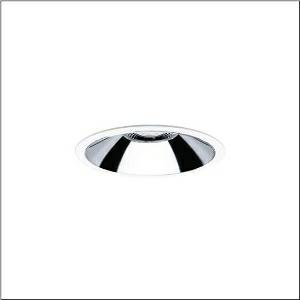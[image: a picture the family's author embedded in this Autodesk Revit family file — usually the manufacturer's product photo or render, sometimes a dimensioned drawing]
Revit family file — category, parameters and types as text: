
# Revit family: lunis_21_xl_51db15df42
name_source: partatom
category: Lighting Fixtures
units: mm (PartAtom-declared; Revit-internal decimal feet)

## family parameters
Cut with Voids When Loaded = No
Host = Face
Light Source = No
Part Type = Normal
Room Calculation Point = No
Round Connector Dimension = Use Diameter
Shared = No

## types (1)
- Lunis 21 XL (1 x LED, 2280 lm, 17.7 W, 4000K)
    Apparent Load = 18 VA
    CIE Flux Codes = 89 99 100 100 100
    Color Rendering = 80
    Color Temperature = 4000K
    Default Elevation = 1800 mm
    Description = Lunis 21,  XL, downlight, of PC, light emission: direct distribution, LED rated luminous flux: 2.280lm, light colour: 840, control gear: ECG DALI, with terminal, 5-pole, mains connection: 220..240V, AC, housing, round, of diecast aluminium, traffic white (RAL 9016), diameter: 213mm, protection rating (complete): IP20, protection rating (on room side): IP54, insulation class (complete): insulation class II (safety insulation), certification: CE, impact resistance: IK02, packaging unit: 1 piece
    Height = 0 mm  [stored 0 ft]
    Lamp = 1 x LED
    Lamp Light Flux = 2280 lm
    Lamp Power = 17.7 W
    Lamp count = 1
    Length = 213 mm
    Luminous efficacy = 129 lm/W
    Manufacturer = Siteco
    ModVariant = No
    Model = 51DB15DF42
    Mounting Place = Ceiling
    Mounting Type = Recessed
    Number of Poles = 1
    OnlyDefault = Yes
    Power Factor = 1
    Product Name = Lunis 21 XL
    Product group = downlight
    ProductGroupID = 401
    Protection Class = Protection class II
    Protection Degree = IP 20
    RLX_Detail_Level = 1
    RLX_Emergency_Light_Flux = 0 lm
    RLX_Emergency_Type = 0
    RLX_Emergency_Type_DB = No
    RlxData = <blob elided: 26937 chars, md5=183c1374>
    Socket = socket
    Standby Power = 0 W
    System Light Flux = 2280 lm
    System Power = 18 W
    Type Comments = Product without accessories
    Type Image = l_1287385.jpg
    URL = http://relux.com
    VarID = ---
    Voltage = 0 V
    Weight = 0.00 kg
    Width = 0 mm  [stored 0 ft]

note: [stored X ft] marks values corroborated as IEEE doubles in the binary element streams (Revit-internal decimal feet)

## geometry (parser evidence)
native form markers: Blend x4, Sweep x11
no freeform markers — native parametric forms only
